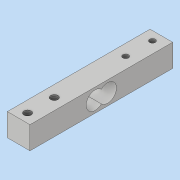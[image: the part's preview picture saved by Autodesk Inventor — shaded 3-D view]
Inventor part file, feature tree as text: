
AUTODESK INVENTOR PART (.ipt)
format: ipt  version: 2018 (Build 220112000, 112)  size: 110,592 bytes
history: native  units: mm
features: sketch x4, extrude x2, hole x2
ambient origin geometry x8: Origin, YZ Plane, XZ Plane, XY Plane, X Axis, Y Axis, Z Axis, Center Point
bodies: Volumenkörper1 (feature_tree)
feature tree (8):
  extrude  "Extrusion1"  Depth=80.0mm
  hole  "Bohrung1"  [1 undecoded]
  hole  "Bohrung2"  [1 undecoded]
  extrude  "Extrusion2"  Depth=12.7mm
  sketch  "Skizze1"  dims[d0=12.7mm d1=80.0mm]
  sketch  "Skizze2"  dims[d2=12.7mm d3=0.0mm d4=5.0mm]
  sketch  "Skizze3"  dims[d5=15.0mm]
  sketch  "Skizze4"  dims[d6=4.134mm d7=10.0mm d8=4.0mm d9=2.0mm d10=90.0deg d11=14.2mm d12=20.594885mm d13=5.0mm d14=15.0mm d15=3.242mm d16=8.0mm d17=4.0mm d18=2.0mm d19=90.0deg d20=11.8mm d21=20.594885mm d22=7.0mm d23=10.0mm d24=10.0mm d25=12.7mm d26=0.0mm]
note: 2 required parameter values undecoded (feature->parameter linkage not recoverable at this tier; creation-order binding heuristic only, values carry confidence <= 0.55)
